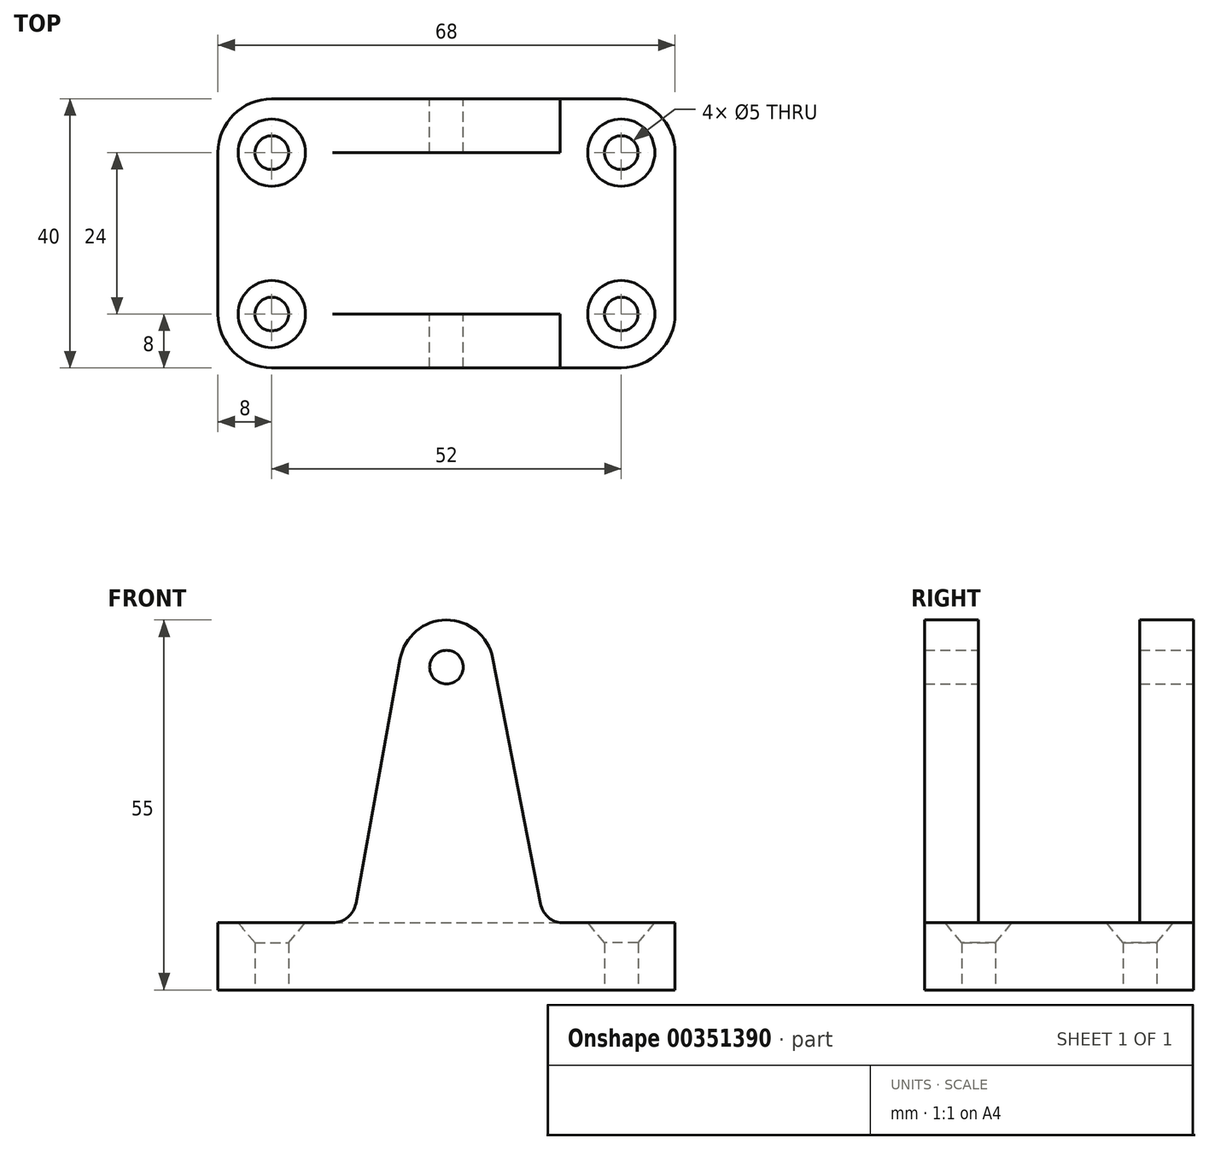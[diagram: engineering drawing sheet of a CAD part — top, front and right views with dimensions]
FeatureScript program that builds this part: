
annotation { "Feature Type Name" : "Feature", "Feature Type Description" : "" }
export const myFeature = defineFeature(function(context is Context, id is Id, definition is map)
    precondition{}
    {
        {
            var Q0;
            Q0=qCreatedBy(makeId("Top.planeOp"),FACE);
            var sketch = newSketch(context, id + "F0", { "sketchPlane" : qUnion([Q0])});
            skLineSegment(sketch, "E0", {"start": v(-26, 40) * mm, "end": v(26, 40) * mm});
            skLineSegment(sketch, "E1", {"start": v(34, 32) * mm, "end": v(34, 8) * mm});
            skLineSegment(sketch, "E2", {"start": v(26, 0) * mm, "end": v(-26, 0) * mm});
            skLineSegment(sketch, "E3", {"start": v(-34, 8) * mm, "end": v(-34, 32) * mm});
            skPoint(sketch, "E4.visualSharp", {"position": v(-34, 40) * mm});
            skArc(sketch, "E4.filletArc", {"start": v(-26, 40) * mm, "mid": v(-31.66, 37.66) * mm, "end": v(-34, 32) * mm});
            skPoint(sketch, "E5.visualSharp", {"position": v(-34, 0) * mm});
            skArc(sketch, "E5.filletArc", {"start": v(-34, 8) * mm, "mid": v(-31.66, 2.34) * mm, "end": v(-26, 0) * mm});
            skPoint(sketch, "E6.visualSharp", {"position": v(34, 0) * mm});
            skArc(sketch, "E6.filletArc", {"start": v(26, 0) * mm, "mid": v(31.66, 2.34) * mm, "end": v(34, 8) * mm});
            skPoint(sketch, "E7.visualSharp", {"position": v(34, 40) * mm});
            skArc(sketch, "E7.filletArc", {"start": v(34, 32) * mm, "mid": v(31.66, 37.66) * mm, "end": v(26, 40) * mm});
            skCircle(sketch, "E8", {"center": v(-26, 32) * mm, "radius": 5 * mm});
            skCircle(sketch, "E9", {"center": v(-26, 8) * mm, "radius": 5 * mm});
            skCircle(sketch, "E10", {"center": v(26, 32) * mm, "radius": 5 * mm});
            skCircle(sketch, "E11", {"center": v(26, 8) * mm, "radius": 5 * mm});
            skCircle(sketch, "E12", {"center": v(-26, 32) * mm, "radius": 2.5 * mm});
            skCircle(sketch, "E13", {"center": v(26, 32) * mm, "radius": 2.5 * mm});
            skCircle(sketch, "E14", {"center": v(26, 8) * mm, "radius": 2.5 * mm});
            skCircle(sketch, "E15", {"center": v(-26, 8) * mm, "radius": 2.5 * mm});
            skSolve(sketch);
        }
        {
            var Q0;
            Q0=makeQuery(id+"F0.imprint","IMPRINT",FACE,{"disambiguationData":[TD([[makeQuery(id+"F0.imprint","IMPRINT",EDGE,{"derivedFrom":sQuery(id+"F0.wireOp",EDGE,"E0")}),-1.0]])]});
            var Q1;
            Q1=makeQuery(id+"F0.imprint","IMPRINT",FACE,{"disambiguationData":[TD([[makeQuery(id+"F0.imprint","IMPRINT",EDGE,{"derivedFrom":sQuery(id+"F0.wireOp",EDGE,"E8")}),1.0]])]});
            var Q2;
            Q2=makeQuery(id+"F0.imprint","IMPRINT",FACE,{"disambiguationData":[TD([[makeQuery(id+"F0.imprint","IMPRINT",EDGE,{"derivedFrom":sQuery(id+"F0.wireOp",EDGE,"E9")}),1.0]])]});
            var Q3;
            Q3=makeQuery(id+"F0.imprint","IMPRINT",FACE,{"disambiguationData":[TD([[makeQuery(id+"F0.imprint","IMPRINT",EDGE,{"derivedFrom":sQuery(id+"F0.wireOp",EDGE,"E11")}),1.0]])]});
            var Q4;
            Q4=makeQuery(id+"F0.imprint","IMPRINT",FACE,{"disambiguationData":[TD([[makeQuery(id+"F0.imprint","IMPRINT",EDGE,{"derivedFrom":sQuery(id+"F0.wireOp",EDGE,"E10")}),1.0]])]});
            var Q5;
            Q5=makeQuery(id+"F0.imprint","IMPRINT",FACE,{"disambiguationData":[TD([[makeQuery(id+"F0.imprint","IMPRINT",EDGE,{"derivedFrom":sQuery(id+"F0.wireOp",EDGE,"E13")}),1.0]])]});
            var Q6;
            Q6=makeQuery(id+"F0.imprint","IMPRINT",FACE,{"disambiguationData":[TD([[makeQuery(id+"F0.imprint","IMPRINT",EDGE,{"derivedFrom":sQuery(id+"F0.wireOp",EDGE,"E14")}),1.0]])]});
            var Q7;
            Q7=makeQuery(id+"F0.imprint","IMPRINT",FACE,{"disambiguationData":[TD([[makeQuery(id+"F0.imprint","IMPRINT",EDGE,{"derivedFrom":sQuery(id+"F0.wireOp",EDGE,"E15")}),1.0]])]});
            var Q8;
            Q8=makeQuery(id+"F0.imprint","IMPRINT",FACE,{"disambiguationData":[TD([[makeQuery(id+"F0.imprint","IMPRINT",EDGE,{"derivedFrom":sQuery(id+"F0.wireOp",EDGE,"E12")}),1.0]])]});
            extrude(context, id + "F1", {"entities" : qUnion([Q0, Q1, Q2, Q3, Q4, Q5, Q6, Q7, Q8]), "depth" : 10 * mm});
        }
        {
            var Q0;
            Q0=makeQuery(id+"F1.opExtrude","SWEPT_FACE",FACE,{"disambiguationData":[OSD([sQuery(id+"F0.wireOp",EDGE,"E0")])]});
            var sketch = newSketch(context, id + "F2", { "sketchPlane" : qUnion([Q0])});
            skLineSegment(sketch, "E16", {"start": v(-34, 10) * mm, "end": v(-34, 0) * mm});
            skLineSegment(sketch, "E17", {"start": v(-34, 0) * mm, "end": v(34, 0) * mm});
            skLineSegment(sketch, "E18", {"start": v(34, 0) * mm, "end": v(34, 10) * mm});
            skLineSegment(sketch, "E19", {"start": v(-18, 10) * mm, "end": v(-34, 10) * mm});
            skCircle(sketch, "E20", {"center": v(0, 48) * mm, "radius": 2.5 * mm});
            skCircle(sketch, "E21", {"center": v(0, 48) * mm, "radius": 7 * mm});
            skLineSegment(sketch, "E22", {"start": v(-14, 12.78) * mm, "end": v(-6.87, 49.34) * mm});
            skLineSegment(sketch, "E23", {"start": v(13.48, 12.88) * mm, "end": v(6.89, 49.25) * mm});
            skPoint(sketch, "E24.orphan", {"position": v(0, 84.57) * mm});
            skPoint(sketch, "E25.newPointA", {"position": v(-14, 12.82) * mm});
            skArc(sketch, "E25.filletArc", {"start": v(-18, 10) * mm, "mid": v(-15.44, 10.58) * mm, "end": v(-14, 12.78) * mm});
            skLineSegment(sketch, "E26", {"start": v(16.92, 10) * mm, "end": v(34, 10) * mm});
            skPoint(sketch, "E27.visualSharp", {"position": v(14, 10) * mm});
            skArc(sketch, "E27.filletArc", {"start": v(13.48, 12.88) * mm, "mid": v(14.68, 10.81) * mm, "end": v(16.92, 10) * mm});
            skLineSegment(sketch, "E28", {"start": v(-26, 10) * mm, "end": v(-26, 7) * mm});
            skPoint(sketch, "E28.endSnap0", {"position": v(-34, 5) * mm});
            skLineSegment(sketch, "E29", {"start": v(-26, 10) * mm, "end": v(-21, 10) * mm});
            skPoint(sketch, "E30.endSnap0", {"position": v(-23.5, 10) * mm});
            skSolve(sketch);
        }
        {
            var Q0;
            {var subQ2=sQuery(id+"F2.wireOp",EDGE,"E22");Q0=makeQuery(id+"F2.imprint","IMPRINT",FACE,{"disambiguationData":[TD([[makeQuery(id+"F2.imprint","IMPRINT",EDGE,{"derivedFrom":subQ2}),-1.0]])]});}
            var Q1;
            Q1=makeQuery(id+"F2.imprint","IMPRINT",FACE,{"disambiguationData":[TD([[makeQuery(id+"F2.imprint","IMPRINT",EDGE,{"derivedFrom":sQuery(id+"F2.wireOp",EDGE,"E20")}),-1.0]])]});
            extrude(context, id + "F3", {"entities" : qUnion([Q0, Q1]), "operationType" : NewBodyOperationType.ADD, "oppositeDirection" : true, "depth" : 8 * mm});
        }
        {
            var Q0;
            {var subQ2=sQuery(id+"F2.wireOp",EDGE,"E22");Q0=makeQuery(id+"F2.imprint","IMPRINT",FACE,{"disambiguationData":[TD([[makeQuery(id+"F2.imprint","IMPRINT",EDGE,{"derivedFrom":subQ2}),-1.0]])]});}
            var Q1;
            Q1=makeQuery(id+"F2.imprint","IMPRINT",FACE,{"disambiguationData":[TD([[makeQuery(id+"F2.imprint","IMPRINT",EDGE,{"derivedFrom":sQuery(id+"F2.wireOp",EDGE,"E20")}),-1.0]])]});
            extrude(context, id + "F4", {"entities" : qUnion([Q0, Q1]), "operationType" : NewBodyOperationType.ADD, "oppositeDirection" : true, "depth" : 40 * mm, "hasSecondDirection" : true, "secondDirectionOppositeDirection" : true, "secondDirectionDepth" : 32 * mm});
        }
        {
            var Q0;
            Q0=makeQuery(id+"F0.imprint","IMPRINT",FACE,{"disambiguationData":[TD([[makeQuery(id+"F0.imprint","IMPRINT",EDGE,{"derivedFrom":sQuery(id+"F0.wireOp",EDGE,"E14")}),1.0]])]});
            var Q1;
            Q1=makeQuery(id+"F0.imprint","IMPRINT",FACE,{"disambiguationData":[TD([[makeQuery(id+"F0.imprint","IMPRINT",EDGE,{"derivedFrom":sQuery(id+"F0.wireOp",EDGE,"E13")}),1.0]])]});
            var Q2;
            Q2=makeQuery(id+"F0.imprint","IMPRINT",FACE,{"disambiguationData":[TD([[makeQuery(id+"F0.imprint","IMPRINT",EDGE,{"derivedFrom":sQuery(id+"F0.wireOp",EDGE,"E12")}),1.0]])]});
            var Q3;
            Q3=makeQuery(id+"F0.imprint","IMPRINT",FACE,{"disambiguationData":[TD([[makeQuery(id+"F0.imprint","IMPRINT",EDGE,{"derivedFrom":sQuery(id+"F0.wireOp",EDGE,"E15")}),1.0]])]});
            extrude(context, id + "F5", {"entities" : qUnion([Q0, Q1, Q2, Q3]), "operationType" : NewBodyOperationType.REMOVE, "depth" : 7 * mm});
        }
        {
            var Q0;
            Q0=makeQuery(id+"F4.boolean.opBoolean","MERGE",FACE,{"derivedFrom":[makeQuery(id+"F1.opExtrude","SWEPT_FACE",FACE,{"disambiguationData":[OSD([sQuery(id+"F0.wireOp",EDGE,"E2")])]}),makeQuery(id+"F4.opExtrude","CAP_FACE",FACE,{"disambiguationData":[OSD([sQuery(id+"F0.wireOp",EDGE,"E0"),sQuery(id+"F2.wireOp",EDGE,"E20"),sQuery(id+"F2.wireOp",EDGE,"E21"),sQuery(id+"F2.wireOp",EDGE,"E22"),sQuery(id+"F2.wireOp",EDGE,"E23"),sQuery(id+"F2.wireOp",EDGE,"E25.filletArc"),sQuery(id+"F2.wireOp",EDGE,"E27.filletArc")])],"isStart":false})]});
            cPlane(context, id + "F6", {"entities" : qUnion([Q0]), "cplaneType" : CPlaneType.OFFSET, "offset" : 8 * mm, "oppositeDirection" : true, "width" : 150 * mm, "height" : 150 * mm});
        }
        {
            var Q0;
            Q0=qCreatedBy(id+"F6.planeOp",FACE);
            var sketch = newSketch(context, id + "F7", { "sketchPlane" : qUnion([Q0])});
            skLineSegment(sketch, "E31", {"start": v(-26, 10) * mm, "end": v(-26, 7) * mm});
            skLineSegment(sketch, "E32", {"start": v(-21, 10) * mm, "end": v(-26, 10) * mm});
            skLineSegment(sketch, "E33", {"start": v(-26, 7) * mm, "end": v(-23.5, 7) * mm});
            skLineSegment(sketch, "E34", {"start": v(-23.5, 7) * mm, "end": v(-21, 10) * mm});
            skSolve(sketch);
        }
        {
            var Q0;
            Q0 = qSketchRegion(id + "F7", true);
            var Q1;
            Q1=sQuery(id+"F7.wireOp",EDGE,"E31");
            revolve(context, id + "F8", {"operationType" : NewBodyOperationType.REMOVE, "entities" : qUnion([Q0]), "axis" : qUnion([Q1]), "revolveType" : RevolveType.FULL, "oppositeDirection" : true});
        }
        {
            var Q0;
            Q0=qCreatedBy(id+"F6.planeOp",FACE);
            var sketch = newSketch(context, id + "F9", { "sketchPlane" : qUnion([Q0])});
            skLineSegment(sketch, "E35.MirrorCS", {"start": v(26, 10) * mm, "end": v(26, 7) * mm});
            skLineSegment(sketch, "E36.MirrorCS", {"start": v(23.5, 7) * mm, "end": v(21, 10) * mm});
            skLineSegment(sketch, "E37.MirrorCS", {"start": v(21, 10) * mm, "end": v(26, 10) * mm});
            skLineSegment(sketch, "E38.MirrorCS", {"start": v(26, 7) * mm, "end": v(23.5, 7) * mm});
            skSolve(sketch);
        }
        {
            var Q0;
            Q0 = qSketchRegion(id + "F9", true);
            var Q1;
            Q1=sQuery(id+"F9.wireOp",EDGE,"E35.MirrorCS");
            revolve(context, id + "F10", {"operationType" : NewBodyOperationType.REMOVE, "entities" : qUnion([Q0]), "axis" : qUnion([Q1]), "revolveType" : RevolveType.FULL});
        }
        {
            var Q0;
            {var subQ0=sQuery(id+"F0.wireOp",EDGE,"E0");Q0=makeQuery(id+"F3.boolean.opBoolean","MERGE",FACE,{"derivedFrom":[makeQuery(id+"F1.opExtrude","SWEPT_FACE",FACE,{"disambiguationData":[OSD([subQ0])]}),makeQuery(id+"F3.opExtrude","CAP_FACE",FACE,{"disambiguationData":[OSD([subQ0,sQuery(id+"F2.wireOp",EDGE,"E20"),sQuery(id+"F2.wireOp",EDGE,"E21"),sQuery(id+"F2.wireOp",EDGE,"E22"),sQuery(id+"F2.wireOp",EDGE,"E23"),sQuery(id+"F2.wireOp",EDGE,"E25.filletArc"),sQuery(id+"F2.wireOp",EDGE,"E27.filletArc")])],"isStart":true})]});}
            cPlane(context, id + "F11", {"entities" : qUnion([Q0]), "cplaneType" : CPlaneType.OFFSET, "offset" : 8 * mm, "oppositeDirection" : true, "width" : 150 * mm, "height" : 150 * mm});
        }
        {
            var Q0;
            Q0=qCreatedBy(id+"F11.planeOp",FACE);
            var sketch = newSketch(context, id + "F12", { "sketchPlane" : qUnion([Q0])});
            skLineSegment(sketch, "E39.MirrorCS", {"start": v(-26, 10) * mm, "end": v(-26, 7) * mm});
            skLineSegment(sketch, "E40.MirrorCS", {"start": v(-28.5, 7) * mm, "end": v(-31, 10) * mm});
            skLineSegment(sketch, "E41.MirrorCS", {"start": v(-31, 10) * mm, "end": v(-26, 10) * mm});
            skLineSegment(sketch, "E42.MirrorCS", {"start": v(-26, 7) * mm, "end": v(-28.5, 7) * mm});
            skSolve(sketch);
        }
        {
            var Q0;
            Q0 = qSketchRegion(id + "F12", true);
            var Q1;
            Q1=sQuery(id+"F12.wireOp",EDGE,"E39.MirrorCS");
            revolve(context, id + "F13", {"operationType" : NewBodyOperationType.REMOVE, "entities" : qUnion([Q0]), "axis" : qUnion([Q1]), "revolveType" : RevolveType.FULL, "oppositeDirection" : true});
        }
        {
            var Q0;
            Q0=qCreatedBy(id+"F11.planeOp",FACE);
            var sketch = newSketch(context, id + "F14", { "sketchPlane" : qUnion([Q0])});
            skLineSegment(sketch, "E43", {"start": v(26, 10) * mm, "end": v(26, 7) * mm});
            skLineSegment(sketch, "E44", {"start": v(31, 10) * mm, "end": v(26, 10) * mm});
            skLineSegment(sketch, "E45", {"start": v(26, 7) * mm, "end": v(28.5, 7) * mm});
            skLineSegment(sketch, "E46", {"start": v(28.5, 7) * mm, "end": v(31, 10) * mm});
            skSolve(sketch);
        }
        {
            var Q0;
            Q0 = qSketchRegion(id + "F14", true);
            var Q1;
            Q1=sQuery(id+"F14.wireOp",EDGE,"E43");
            revolve(context, id + "F15", {"operationType" : NewBodyOperationType.REMOVE, "entities" : qUnion([Q0]), "axis" : qUnion([Q1]), "revolveType" : RevolveType.FULL, "oppositeDirection" : true});
        }
    });
